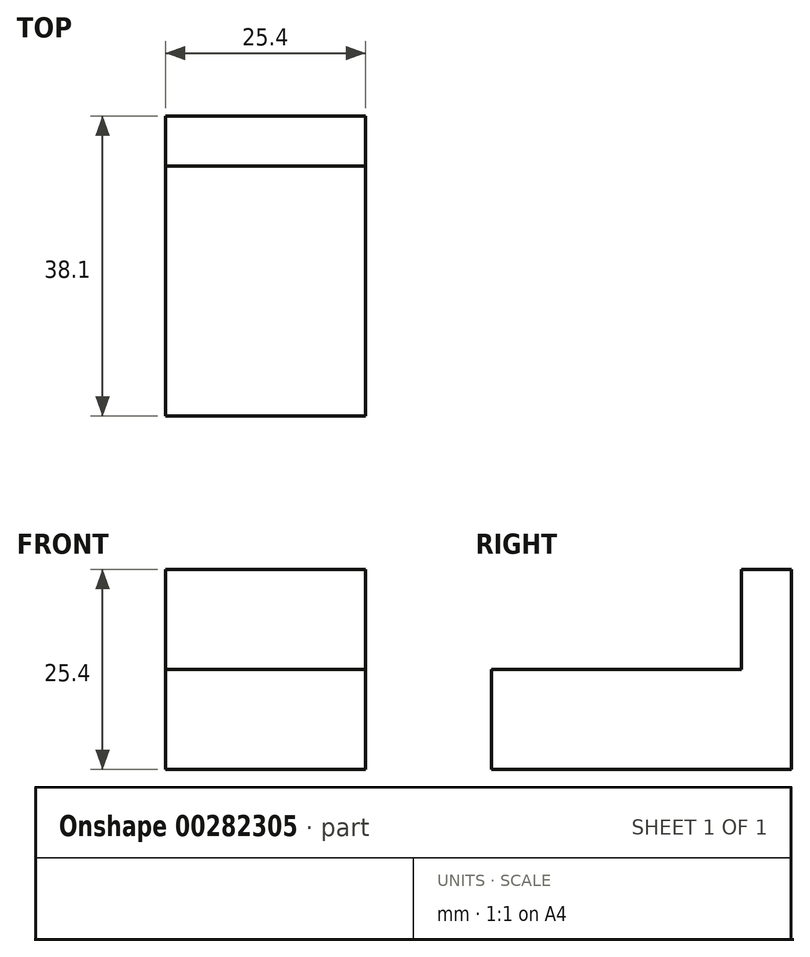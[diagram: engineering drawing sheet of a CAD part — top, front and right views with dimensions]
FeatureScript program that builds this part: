
annotation { "Feature Type Name" : "Feature", "Feature Type Description" : "" }
export const myFeature = defineFeature(function(context is Context, id is Id, definition is map)
    precondition{}
    {
        {
            var Q0;
            Q0=qCreatedBy(makeId("Front.planeOp"),FACE);
            var sketch = newSketch(context, id + "F0", { "sketchPlane" : qUnion([Q0])});
            skLineSegment(sketch, "E0", {"start": v(0, 0) * mm, "end": v(25.4, 0) * mm});
            skLineSegment(sketch, "E1", {"start": v(25.4, 0) * mm, "end": v(25.4, 12.7) * mm});
            skLineSegment(sketch, "E2", {"start": v(25.4, 12.7) * mm, "end": v(0, 12.7) * mm});
            skLineSegment(sketch, "E3", {"start": v(0, 12.7) * mm, "end": v(0, 0) * mm});
            skSolve(sketch);
        }
        {
            var Q0;
            Q0 = qSketchRegion(id + "F0", true);
            extrude(context, id + "F1", {"entities" : qUnion([Q0]), "depth" : 38.1 * mm});
        }
        {
            var Q0;
            Q0=makeQuery(id+"F1.opExtrude","SWEPT_FACE",FACE,{"disambiguationData":[OSD([sQuery(id+"F0.wireOp",EDGE,"E2")])]});
            var sketch = newSketch(context, id + "F2", { "sketchPlane" : qUnion([Q0])});
            skLineSegment(sketch, "E4", {"start": v(25.4, 0) * mm, "end": v(25.4, -6.35) * mm});
            skLineSegment(sketch, "E5", {"start": v(25.4, -6.35) * mm, "end": v(0, -6.35) * mm});
            skLineSegment(sketch, "E6", {"start": v(0, -6.35) * mm, "end": v(0, 0) * mm});
            skLineSegment(sketch, "E7", {"start": v(0, 0) * mm, "end": v(25.4, 0) * mm});
            skSolve(sketch);
        }
        {
            var Q0;
            Q0=makeQuery(id+"F2.imprint","IMPRINT",FACE,{"disambiguationData":[TD([[makeQuery(id+"F2.imprint","IMPRINT",EDGE,{"derivedFrom":sQuery(id+"F2.wireOp",EDGE,"E4")}),1.0]])]});
            extrude(context, id + "F3", {"entities" : qUnion([Q0]), "operationType" : NewBodyOperationType.ADD, "depth" : 12.7 * mm});
        }
    });
